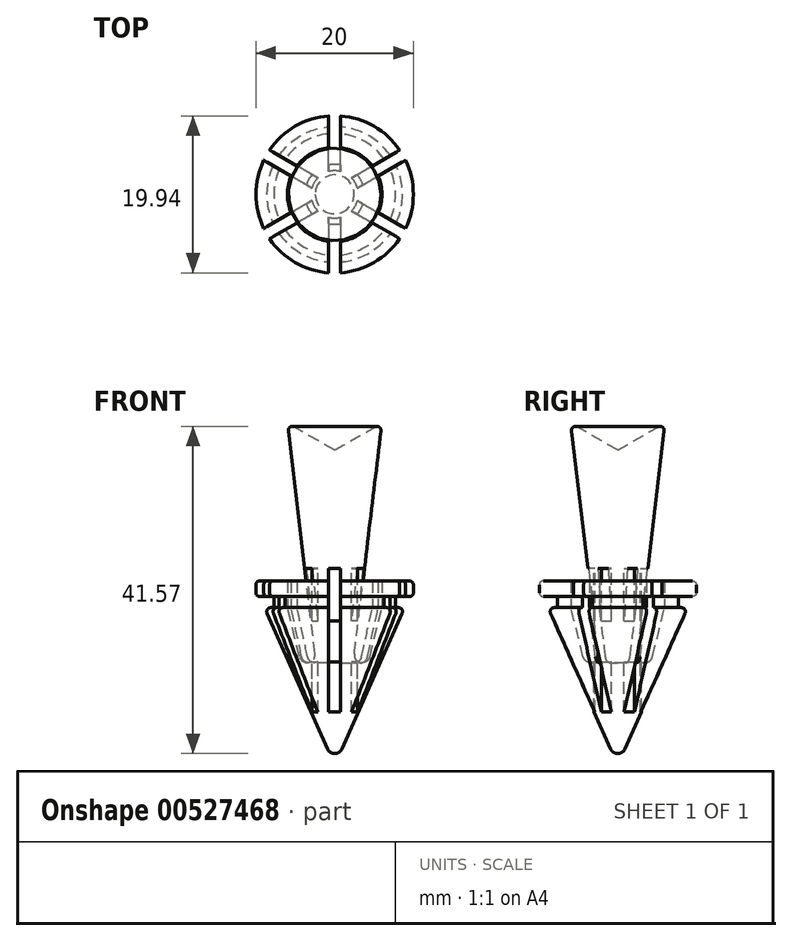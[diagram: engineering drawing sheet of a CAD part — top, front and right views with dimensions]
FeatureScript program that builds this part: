
annotation { "Feature Type Name" : "Feature", "Feature Type Description" : "" }
export const myFeature = defineFeature(function(context is Context, id is Id, definition is map)
    precondition{}
    {
        {
            var Q0;
            Q0=qCreatedBy(makeId("Front.planeOp"),FACE);
            var sketch = newSketch(context, id + "F0", { "sketchPlane" : qUnion([Q0])});
            skLineSegment(sketch, "E0", {"start": v(0, 1.46) * mm, "end": v(0, 40) * mm});
            skLineSegment(sketch, "E1", {"start": v(0, 40) * mm, "end": v(-6, 43.46) * mm});
            skLineSegment(sketch, "E2", {"start": v(-7.73, 20) * mm, "end": v(-8.12, 20) * mm});
            skLineSegment(sketch, "E3", {"start": v(-8.58, 19.3) * mm, "end": v(-0.91, 2.05) * mm});
            skLineSegment(sketch, "E4", {"start": v(-7.62, 23.56) * mm, "end": v(-7.62, 0) * mm, "construction": true});
            skArc(sketch, "E5", {"start": v(-0.91, 2.05) * mm, "mid": v(-0.54, 1.62) * mm, "end": v(0, 1.46) * mm});
            skPoint(sketch, "E6.orphan", {"position": v(0, 0) * mm});
            skPoint(sketch, "E7.visualSharp", {"position": v(-8.9, 20) * mm});
            skArc(sketch, "E7.filletArc", {"start": v(-8.12, 20) * mm, "mid": v(-8.54, 19.77) * mm, "end": v(-8.58, 19.3) * mm});
            skLineSegment(sketch, "E8", {"start": v(-7.73, 20) * mm, "end": v(-7.73, 21.4) * mm});
            skLineSegment(sketch, "E9", {"start": v(-7.73, 21.4) * mm, "end": v(-10, 21.4) * mm});
            skLineSegment(sketch, "E10", {"start": v(-10, 21.4) * mm, "end": v(-10, 23.4) * mm});
            skLineSegment(sketch, "E11", {"start": v(-10, 23.4) * mm, "end": v(-6, 23.4) * mm});
            skLineSegment(sketch, "E12", {"start": v(-6, 23.4) * mm, "end": v(-6, 20) * mm});
            skLineSegment(sketch, "E13", {"start": v(-6, 20) * mm, "end": v(-4.46, 13.77) * mm});
            skArc(sketch, "E14.filletArc", {"start": v(-4.46, 13.77) * mm, "mid": v(-3.31, 13.02) * mm, "end": v(-2.5, 14.12) * mm});
            skLineSegment(sketch, "E15", {"start": v(-2.5, 14.12) * mm, "end": v(-6, 43.46) * mm});
            skSolve(sketch);
        }
        {
            var Q0;
            Q0=makeQuery(id+"F0.imprint","IMPRINT",FACE,{"disambiguationData":[TD([[makeQuery(id+"F0.imprint","IMPRINT",EDGE,{"derivedFrom":sQuery(id+"F0.wireOp",EDGE,"E0")}),1.0]])]});
            var Q1;
            Q1=sQuery(id+"F0.wireOp",EDGE,"E0");
            revolve(context, id + "F1", {"entities" : qUnion([Q0]), "axis" : qUnion([Q1]), "revolveType" : RevolveType.FULL});
        }
        {
            var Q0;
            Q0=makeQuery(id+"F1.opRevolve","SWEPT_EDGE",EDGE,{"disambiguationData":[OSD([sQuery(id+"F0.wireOp",EDGE,"E10"),sQuery(id+"F0.wireOp",EDGE,"E11")])]});
            var Q1;
            Q1=makeQuery(id+"F1.opRevolve","SWEPT_EDGE",EDGE,{"disambiguationData":[OSD([sQuery(id+"F0.wireOp",EDGE,"E9"),sQuery(id+"F0.wireOp",EDGE,"E10")])]});
            var Q2;
            Q2=makeQuery(id+"F1.opRevolve","SWEPT_EDGE",EDGE,{"disambiguationData":[OSD([sQuery(id+"F0.wireOp",EDGE,"E1"),sQuery(id+"F0.wireOp",EDGE,"E15")])]});
            fillet(context, id + "F2", {"entities" : qUnion([Q0, Q1, Q2]), "radius" : 0.5 * mm, "tangentPropagation" : true, "allowEdgeOverflow" : false});
        }
        {
            var Q0;
            Q0=qCreatedBy(makeId("Top.planeOp"),FACE);
            var sketch = newSketch(context, id + "F3", { "sketchPlane" : qUnion([Q0])});
            skLineSegment(sketch, "E16", {"start": v(0, 0) * mm, "end": v(0, 18.4) * mm, "construction": true});
            skLineSegment(sketch, "E17.top", {"start": v(0.75, 10.83) * mm, "end": v(-0.75, 10.83) * mm});
            skLineSegment(sketch, "E17.left", {"start": v(0.75, 2.9) * mm, "end": v(0.75, 10.83) * mm});
            skLineSegment(sketch, "E17.right", {"start": v(-0.75, 2.9) * mm, "end": v(-0.75, 10.83) * mm});
            skPoint(sketch, "E17.middle", {"position": v(0, 6.87) * mm});
            skArc(sketch, "E18.0", {"start": v(0.75, 2.9) * mm, "mid": v(0, 3) * mm, "end": v(-0.75, 2.9) * mm});
            skLineSegment(sketch, "E19.1.0", {"start": v(-2.14, 2.1) * mm, "end": v(-9, 6.07) * mm});
            skLineSegment(sketch, "E19.1.1", {"start": v(-2.9, 0.8) * mm, "end": v(-9.76, 4.77) * mm});
            skArc(sketch, "E19.1.2", {"start": v(-2.14, 2.1) * mm, "mid": v(-2.6, 1.5) * mm, "end": v(-2.9, 0.8) * mm});
            skPoint(sketch, "E19.1.3", {"position": v(-5.95, 3.43) * mm});
            skLineSegment(sketch, "E19.1.4", {"start": v(-9, 6.07) * mm, "end": v(-9.76, 4.77) * mm});
            skLineSegment(sketch, "E19.2.0", {"start": v(-2.9, -0.8) * mm, "end": v(-9.76, -4.77) * mm});
            skLineSegment(sketch, "E19.2.1", {"start": v(-2.14, -2.1) * mm, "end": v(-9, -6.07) * mm});
            skArc(sketch, "E19.2.2", {"start": v(-2.9, -0.8) * mm, "mid": v(-2.6, -1.5) * mm, "end": v(-2.14, -2.1) * mm});
            skPoint(sketch, "E19.2.3", {"position": v(-5.95, -3.43) * mm});
            skLineSegment(sketch, "E19.2.4", {"start": v(-9.76, -4.77) * mm, "end": v(-9, -6.07) * mm});
            skLineSegment(sketch, "E20.3.3.0", {"start": v(0.75, -2.9) * mm, "end": v(0.75, -10.83) * mm});
            skLineSegment(sketch, "E20.4.3.0", {"start": v(-0.75, -2.9) * mm, "end": v(-0.75, -10.83) * mm});
            skArc(sketch, "E20.6.3.0", {"start": v(-0.75, -2.9) * mm, "mid": v(0, -3) * mm, "end": v(0.75, -2.9) * mm});
            skPoint(sketch, "E20.10.3.0", {"position": v(0, -6.87) * mm});
            skLineSegment(sketch, "E20.11.3.0", {"start": v(-0.75, -10.83) * mm, "end": v(0.75, -10.83) * mm});
            skLineSegment(sketch, "E20.3.4.0", {"start": v(2.9, -0.8) * mm, "end": v(9.76, -4.77) * mm});
            skLineSegment(sketch, "E20.4.4.0", {"start": v(2.14, -2.1) * mm, "end": v(9, -6.07) * mm});
            skArc(sketch, "E20.6.4.0", {"start": v(2.14, -2.1) * mm, "mid": v(2.6, -1.5) * mm, "end": v(2.9, -0.8) * mm});
            skPoint(sketch, "E20.10.4.0", {"position": v(5.95, -3.43) * mm});
            skLineSegment(sketch, "E20.11.4.0", {"start": v(9, -6.07) * mm, "end": v(9.76, -4.77) * mm});
            skLineSegment(sketch, "E20.3.5.0", {"start": v(2.14, 2.1) * mm, "end": v(9, 6.07) * mm});
            skLineSegment(sketch, "E20.4.5.0", {"start": v(2.9, 0.8) * mm, "end": v(9.76, 4.77) * mm});
            skArc(sketch, "E20.6.5.0", {"start": v(2.9, 0.8) * mm, "mid": v(2.6, 1.5) * mm, "end": v(2.14, 2.1) * mm});
            skPoint(sketch, "E20.10.5.0", {"position": v(5.95, 3.43) * mm});
            skLineSegment(sketch, "E20.11.5.0", {"start": v(9.76, 4.77) * mm, "end": v(9, 6.07) * mm});
            skSolve(sketch);
        }
        {
            var Q0;
            Q0=qSketchRegion(id+"F3",true);
            extrude(context, id + "F4", {"entities" : qUnion([Q0]), "operationType" : NewBodyOperationType.REMOVE, "oppositeDirection" : true, "depth" : 25 * mm, "offsetDistance" : 25 * mm, "hasSecondDirection" : true, "secondDirectionOppositeDirection" : false, "secondDirectionDepth" : 25 * mm});
        }
    });
